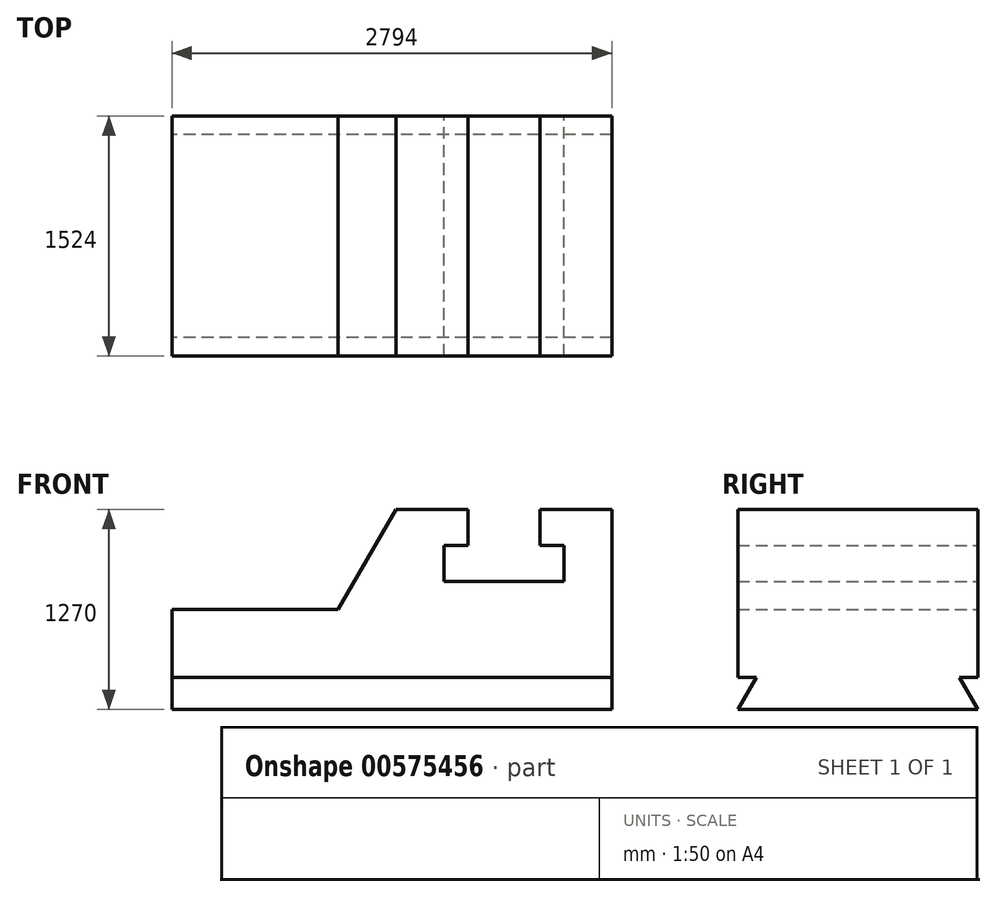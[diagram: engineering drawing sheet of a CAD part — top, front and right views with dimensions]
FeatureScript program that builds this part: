
annotation { "Feature Type Name" : "Feature", "Feature Type Description" : "" }
export const myFeature = defineFeature(function(context is Context, id is Id, definition is map)
    precondition{}
    {
        {
            var Q0;
            Q0=qCreatedBy(makeId("Front.planeOp"),FACE);
            var sketch = newSketch(context, id + "F0", { "sketchPlane" : qUnion([Q0])});
            skLineSegment(sketch, "E0", {"start": v(0, 0) * mm, "end": v(2794, 0) * mm});
            skLineSegment(sketch, "E1", {"start": v(2794, 0) * mm, "end": v(2794, 1270) * mm});
            skLineSegment(sketch, "E2", {"start": v(2794, 1270) * mm, "end": v(2336.8, 1270) * mm});
            skLineSegment(sketch, "E3", {"start": v(2336.8, 1270) * mm, "end": v(2336.8, 1041.4) * mm});
            skLineSegment(sketch, "E4", {"start": v(2336.8, 1041.4) * mm, "end": v(2489.2, 1041.4) * mm});
            skLineSegment(sketch, "E5", {"start": v(2489.2, 1041.4) * mm, "end": v(2489.2, 812.8) * mm});
            skLineSegment(sketch, "E6", {"start": v(2489.2, 812.8) * mm, "end": v(1727.2, 812.8) * mm});
            skLineSegment(sketch, "E7", {"start": v(1727.2, 812.8) * mm, "end": v(1727.2, 1041.4) * mm});
            skLineSegment(sketch, "E8", {"start": v(1727.2, 1041.4) * mm, "end": v(1879.6, 1041.4) * mm});
            skLineSegment(sketch, "E9", {"start": v(1879.6, 1041.4) * mm, "end": v(1879.6, 1270) * mm});
            skLineSegment(sketch, "E10", {"start": v(1879.6, 1270) * mm, "end": v(1422.4, 1270) * mm});
            skLineSegment(sketch, "E11", {"start": v(1422.4, 1270) * mm, "end": v(1055.78, 635) * mm});
            skLineSegment(sketch, "E12", {"start": v(1055.78, 635) * mm, "end": v(0, 635) * mm});
            skLineSegment(sketch, "E13", {"start": v(0, 635) * mm, "end": v(0, 0) * mm});
            skSolve(sketch);
        }
        {
            var Q0;
            Q0=makeQuery(id+"F0.imprint","IMPRINT",FACE,{"disambiguationData":[TD([[makeQuery(id+"F0.imprint","IMPRINT",EDGE,{"derivedFrom":sQuery(id+"F0.wireOp",EDGE,"E0")}),1.0]])]});
            extrude(context, id + "F1", {"entities" : qUnion([Q0]), "depth" : 1524 * mm, "offsetDistance" : 25.4 * mm});
        }
        {
            var Q0;
            Q0=makeQuery(id+"F1.opExtrude","SWEPT_FACE",FACE,{"disambiguationData":[OSD([sQuery(id+"F0.wireOp",EDGE,"E13")])]});
            var sketch = newSketch(context, id + "F2", { "sketchPlane" : qUnion([Q0])});
            skLineSegment(sketch, "E14", {"start": v(0, 0) * mm, "end": v(0, 203.2) * mm});
            skLineSegment(sketch, "E15", {"start": v(0, 203.2) * mm, "end": v(117.32, 203.2) * mm});
            skLineSegment(sketch, "E16", {"start": v(117.32, 203.2) * mm, "end": v(0, 0) * mm});
            skSolve(sketch);
        }
        {
            var Q0;
            Q0=makeQuery(id+"F2.imprint","IMPRINT",FACE,{"disambiguationData":[TD([[makeQuery(id+"F2.imprint","IMPRINT",EDGE,{"derivedFrom":sQuery(id+"F2.wireOp",EDGE,"E14")}),1.0]])]});
            extrude(context, id + "F3", {"entities" : qUnion([Q0]), "operationType" : NewBodyOperationType.REMOVE, "endBound" : BoundingType.THROUGH_ALL, "oppositeDirection" : true, "depth" : 25.4 * mm, "offsetDistance" : 25.4 * mm});
        }
        {
            var Q0;
            Q0=makeQuery(id+"F1.opExtrude","SWEPT_FACE",FACE,{"disambiguationData":[OSD([sQuery(id+"F0.wireOp",EDGE,"E13")])]});
            var sketch = newSketch(context, id + "F4", { "sketchPlane" : qUnion([Q0])});
            skLineSegment(sketch, "E17", {"start": v(1524, 0) * mm, "end": v(1524, 203.2) * mm});
            skLineSegment(sketch, "E18", {"start": v(1524, 203.2) * mm, "end": v(1406.68, 203.2) * mm});
            skLineSegment(sketch, "E19", {"start": v(1406.68, 203.2) * mm, "end": v(1524, 0) * mm});
            skSolve(sketch);
        }
        {
            var Q0;
            Q0=makeQuery(id+"F4.imprint","IMPRINT",FACE,{"disambiguationData":[TD([[makeQuery(id+"F4.imprint","IMPRINT",EDGE,{"derivedFrom":sQuery(id+"F4.wireOp",EDGE,"E17")}),-1.0]])]});
            extrude(context, id + "F5", {"entities" : qUnion([Q0]), "operationType" : NewBodyOperationType.REMOVE, "endBound" : BoundingType.THROUGH_ALL, "oppositeDirection" : true, "depth" : 25.4 * mm, "offsetDistance" : 25.4 * mm});
        }
    });
